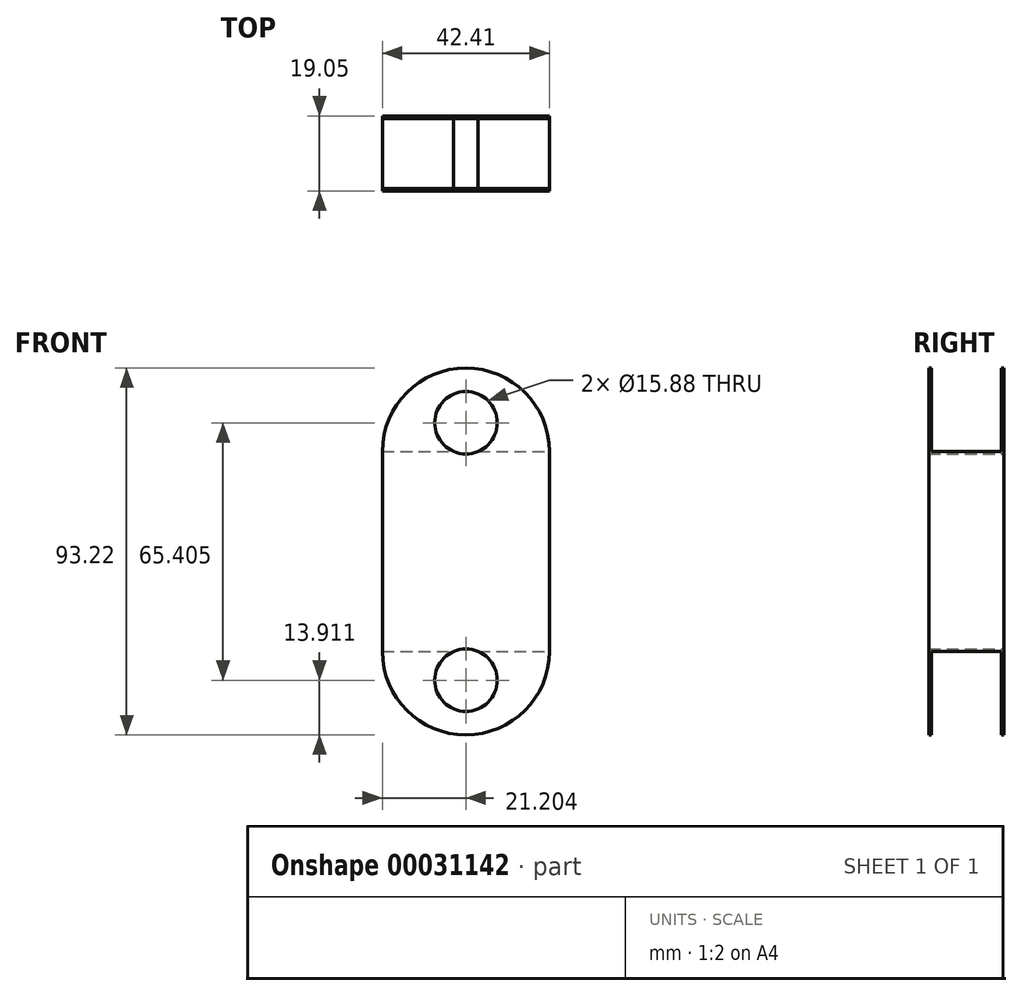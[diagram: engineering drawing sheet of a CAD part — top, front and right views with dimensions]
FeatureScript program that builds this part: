
annotation { "Feature Type Name" : "Feature", "Feature Type Description" : "" }
export const myFeature = defineFeature(function(context is Context, id is Id, definition is map)
    precondition{}
    {
        {
            var Q0;
            Q0=qCreatedBy(makeId("Front.planeOp"),FACE);
            var sketch = newSketch(context, id + "F0", { "sketchPlane" : qUnion([Q0])});
            skLineSegment(sketch, "E0.bottom", {"start": v(-10.4, 67.63) * mm, "end": v(32.01, 67.63) * mm});
            skLineSegment(sketch, "E0.top", {"start": v(-10.4, 16.83) * mm, "end": v(32.01, 16.83) * mm});
            skLineSegment(sketch, "E0.left", {"start": v(-10.4, 67.63) * mm, "end": v(-10.4, 16.83) * mm});
            skLineSegment(sketch, "E0.right", {"start": v(32.01, 67.63) * mm, "end": v(32.01, 16.83) * mm});
            skArc(sketch, "E1", {"start": v(32.01, 67.63) * mm, "mid": v(10.8, 88.84) * mm, "end": v(-10.4, 67.63) * mm});
            skArc(sketch, "E2", {"start": v(-10.4, 16.83) * mm, "mid": v(10.8, -4.38) * mm, "end": v(32.01, 16.83) * mm});
            skCircle(sketch, "E3", {"center": v(10.8, 74.94) * mm, "radius": 7.94 * mm});
            skCircle(sketch, "E4", {"center": v(10.8, 9.53) * mm, "radius": 7.94 * mm});
            skSolve(sketch);
        }
        {
            var Q0;
            {var subQ4=sQuery(id+"F0.wireOp",EDGE,"E0.left");Q0=makeQuery(id+"F0.imprint","IMPRINT",FACE,{"disambiguationData":[TD([[makeQuery(id+"F0.imprint","IMPRINT",EDGE,{"derivedFrom":subQ4}),1.0]])]});}
            extrude(context, id + "F1", {"entities" : qUnion([Q0]), "depth" : 19.05 * mm});
        }
        {
            var Q0;
            Q0 = qSketchRegion(id + "F0", true);
            extrude(context, id + "F2", {"entities" : qUnion([Q0]), "operationType" : NewBodyOperationType.ADD, "depth" : 0.64 * mm});
        }
        {
            var Q0;
            Q0=makeQuery(id+"F1.opExtrude","CAP_FACE",FACE,{"disambiguationData":[OSD([sQuery(id+"F0.wireOp",EDGE,"E0.bottom"),sQuery(id+"F0.wireOp",EDGE,"E0.top"),sQuery(id+"F0.wireOp",EDGE,"E0.left"),sQuery(id+"F0.wireOp",EDGE,"E0.right"),sQuery(id+"F0.wireOp",EDGE,"E3"),sQuery(id+"F0.wireOp",EDGE,"E4")])],"isStart":false});
            var sketch = newSketch(context, id + "F3", { "sketchPlane" : qUnion([Q0])});
            skArc(sketch, "E5", {"start": v(32.01, 67.63) * mm, "mid": v(10.8, 88.84) * mm, "end": v(-10.4, 67.63) * mm});
            skCircle(sketch, "E6", {"center": v(10.8, 74.94) * mm, "radius": 7.94 * mm});
            skArc(sketch, "E7", {"start": v(-10.4, 16.83) * mm, "mid": v(10.8, -4.38) * mm, "end": v(32.01, 16.83) * mm});
            skCircle(sketch, "E8", {"center": v(10.8, 9.53) * mm, "radius": 7.94 * mm});
            skSolve(sketch);
        }
        {
            var Q0;
            Q0=makeQuery(id+"F3.imprint","IMPRINT",FACE,{"disambiguationData":[TD([[makeQuery(id+"F3.imprint","IMPRINT",EDGE,{"derivedFrom":sQuery(id+"F3.wireOp",EDGE,"E7")}),1.0]])]});
            var Q1;
            Q1=makeQuery(id+"F3.imprint","IMPRINT",FACE,{"disambiguationData":[TD([[makeQuery(id+"F3.imprint","IMPRINT",EDGE,{"derivedFrom":sQuery(id+"F3.wireOp",EDGE,"E5")}),1.0]])]});
            extrude(context, id + "F4", {"entities" : qUnion([Q0, Q1]), "operationType" : NewBodyOperationType.ADD, "oppositeDirection" : true, "depth" : 0.64 * mm});
        }
    });
